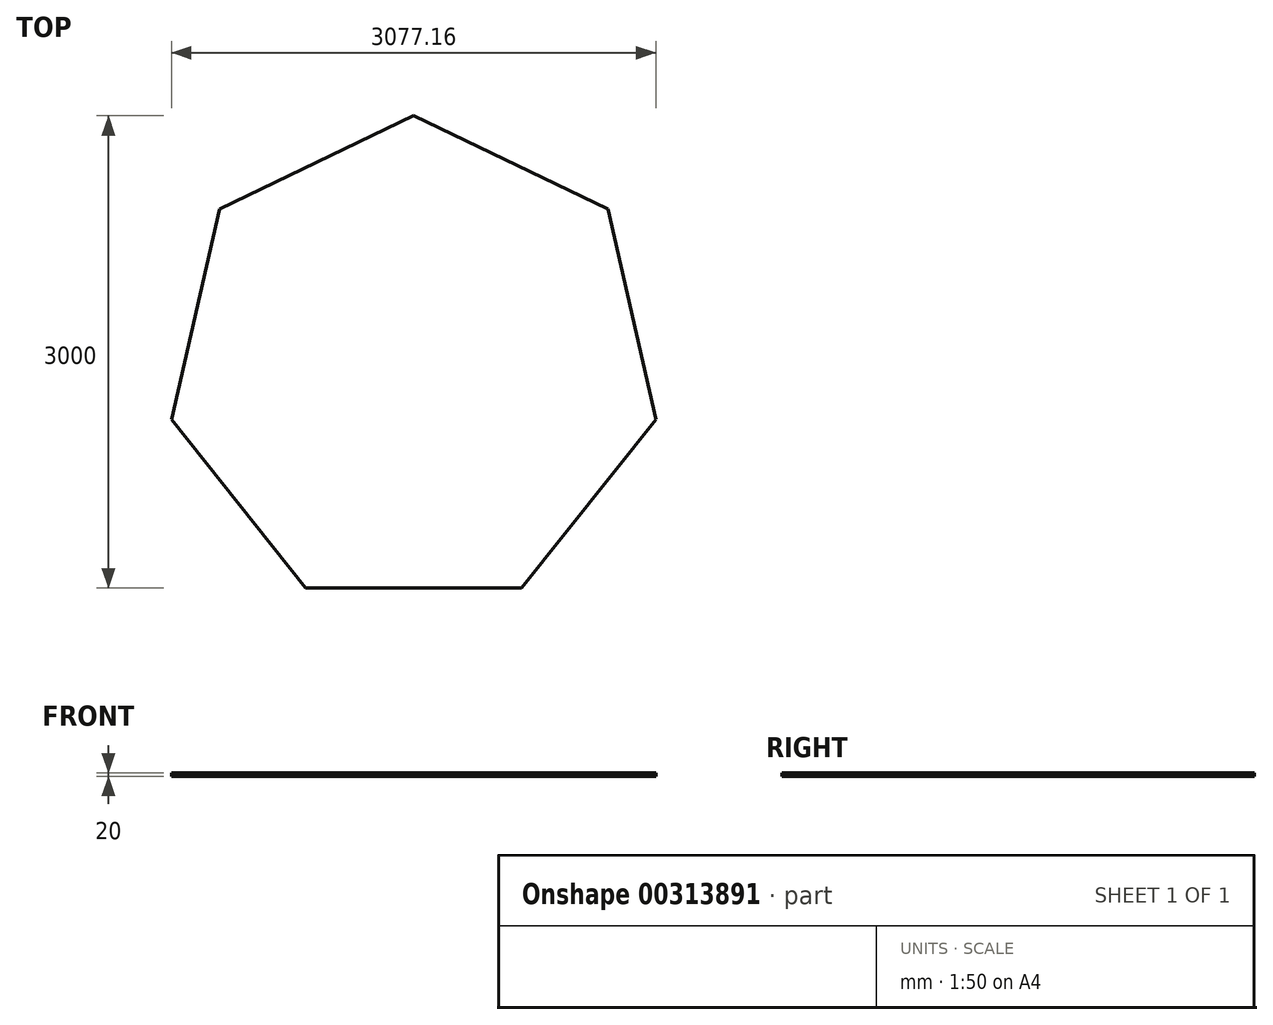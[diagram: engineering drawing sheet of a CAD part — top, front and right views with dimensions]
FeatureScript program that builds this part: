
annotation { "Feature Type Name" : "Feature", "Feature Type Description" : "" }
export const myFeature = defineFeature(function(context is Context, id is Id, definition is map)
    precondition{}
    {
        {
            var Q0;
            Q0=qCreatedBy(makeId("Top.planeOp"),FACE);
            var sketch = newSketch(context, id + "F0", { "sketchPlane" : qUnion([Q0])});
            skCircle(sketch, "E0.cCircle", {"center": v(0, 0) * mm, "radius": 1578.14 * mm, "construction": true});
            skLineSegment(sketch, "E0.0", {"start": v(0, 1578.14) * mm, "end": v(1233.84, 983.96) * mm});
            skLineSegment(sketch, "E0.1", {"start": v(1233.84, 983.96) * mm, "end": v(1538.58, -351.17) * mm});
            skLineSegment(sketch, "E0.2", {"start": v(1538.58, -351.17) * mm, "end": v(684.73, -1421.86) * mm});
            skLineSegment(sketch, "E0.3", {"start": v(684.73, -1421.86) * mm, "end": v(-684.73, -1421.86) * mm});
            skLineSegment(sketch, "E0.4", {"start": v(-684.73, -1421.86) * mm, "end": v(-1538.58, -351.17) * mm});
            skLineSegment(sketch, "E0.5", {"start": v(-1538.58, -351.17) * mm, "end": v(-1233.84, 983.96) * mm});
            skLineSegment(sketch, "E0.6", {"start": v(-1233.84, 983.96) * mm, "end": v(0, 1578.14) * mm});
            skSolve(sketch);
        }
        {
            var Q0;
            Q0=makeQuery(id+"F0.imprint","IMPRINT",FACE,{"disambiguationData":[TD([[makeQuery(id+"F0.imprint","IMPRINT",EDGE,{"derivedFrom":sQuery(id+"F0.wireOp",EDGE,"E0.0")}),-1.0]])]});
            extrude(context, id + "F1", {"entities" : qUnion([Q0]), "depth" : 20 * mm});
        }
    });
